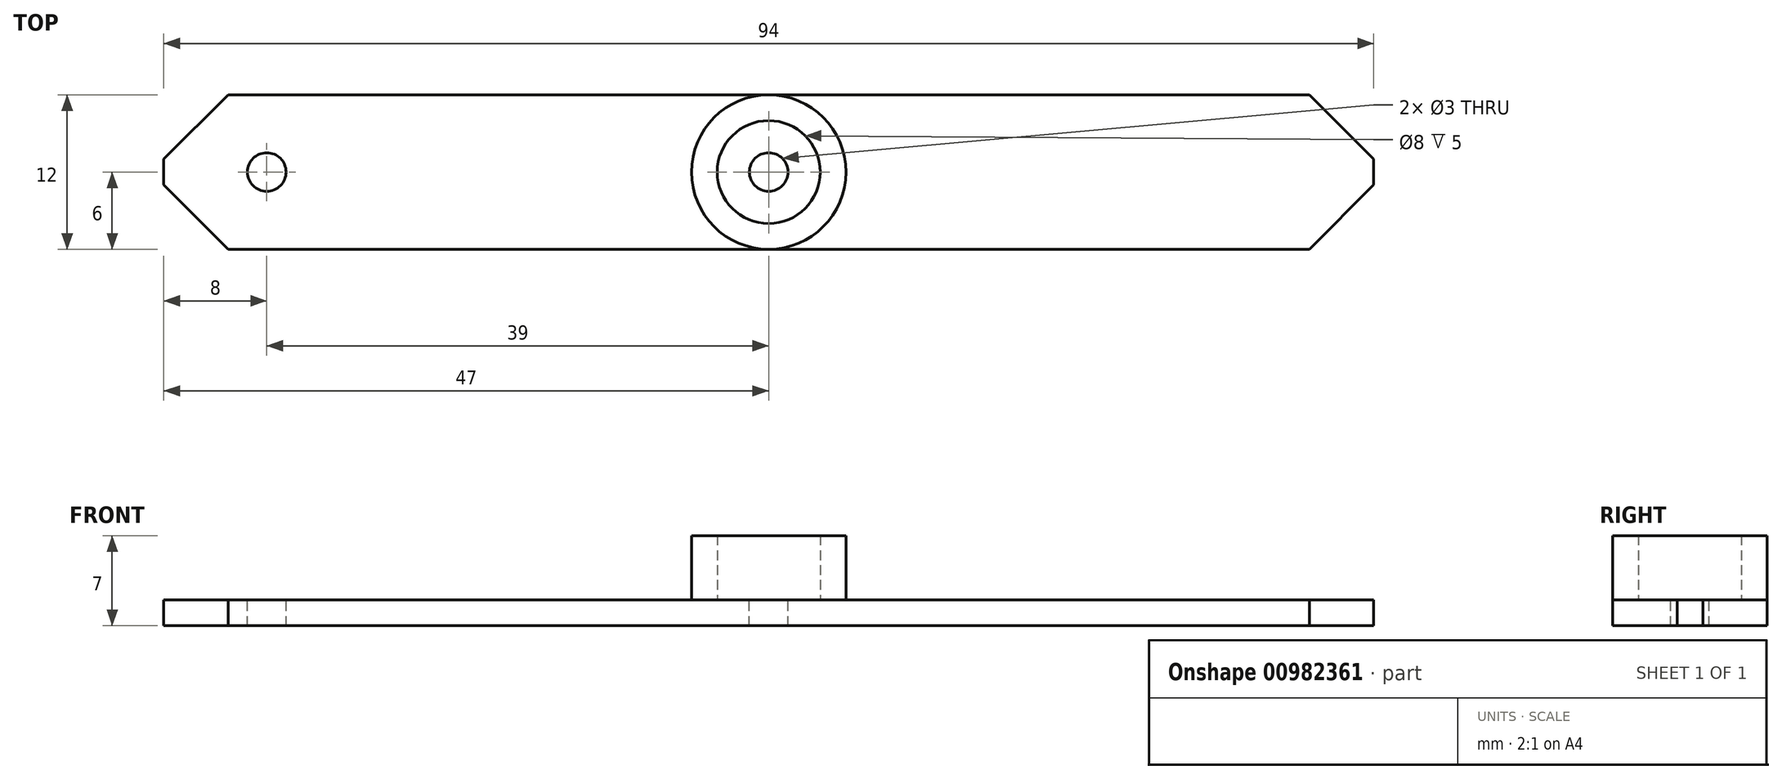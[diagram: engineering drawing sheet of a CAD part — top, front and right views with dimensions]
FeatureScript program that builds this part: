
annotation { "Feature Type Name" : "Feature", "Feature Type Description" : "" }
export const myFeature = defineFeature(function(context is Context, id is Id, definition is map)
    precondition{}
    {
        {
            var Q0;
            Q0=qCreatedBy(makeId("Top.planeOp"),FACE);
            var sketch = newSketch(context, id + "F0", { "sketchPlane" : qUnion([Q0])});
            skLineSegment(sketch, "E0.bottom", {"start": v(0, 0) * mm, "end": v(-94, 0) * mm});
            skLineSegment(sketch, "E0.top", {"start": v(0, -12) * mm, "end": v(-94, -12) * mm});
            skLineSegment(sketch, "E0.left", {"start": v(0, 0) * mm, "end": v(0, -12) * mm});
            skLineSegment(sketch, "E0.right", {"start": v(-94, 0) * mm, "end": v(-94, -12) * mm});
            skSolve(sketch);
        }
        {
            var Q0;
            Q0 = qSketchRegion(id + "F0", true);
            extrude(context, id + "F1", {"entities" : qUnion([Q0]), "depth" : 2 * mm, "offsetDistance" : 25 * mm});
        }
        {
            var Q0;
            Q0=makeQuery(id+"F1.opExtrude","CAP_FACE",FACE,{"disambiguationData":[OSD([sQuery(id+"F0.wireOp",EDGE,"E0.bottom"),sQuery(id+"F0.wireOp",EDGE,"E0.top"),sQuery(id+"F0.wireOp",EDGE,"E0.left"),sQuery(id+"F0.wireOp",EDGE,"E0.right")])],"isStart":false});
            var sketch = newSketch(context, id + "F2", { "sketchPlane" : qUnion([Q0])});
            skCircle(sketch, "E1", {"center": v(-47, -6) * mm, "radius": 6 * mm});
            skPoint(sketch, "E1.centerSnap0", {"position": v(-47, 0) * mm});
            skPoint(sketch, "E1.centerSnap1", {"position": v(0, -6) * mm});
            skSolve(sketch);
        }
        {
            var Q0;
            {var subQ0=sQuery(id+"F2.wireOp",EDGE,"E1");var subQ1=makeQuery(id+"F2.imprint","INTERSECT",VERTEX,{"derivedFrom":[makeQuery(id+"F1.opExtrude","CAP_EDGE",EDGE,{"disambiguationData":[OSD([sQuery(id+"F0.wireOp",EDGE,"E0.bottom")])],"isStart":false}),subQ0]});Q0=makeQuery(id+"F2.imprint","IMPRINT",FACE,{"disambiguationData":[TD([[makeQuery(id+"F2.imprint","IMPRINT",EDGE,{"disambiguationData":[TD([[subQ1,-1.0]])],"derivedFrom":subQ0}),1.0]])]});}
            extrude(context, id + "F3", {"entities" : qUnion([Q0]), "operationType" : NewBodyOperationType.ADD, "depth" : 5 * mm, "offsetDistance" : 25 * mm});
        }
        {
            var Q0;
            Q0=makeQuery(id+"F3.opExtrude","CAP_FACE",FACE,{"disambiguationData":[OSD([sQuery(id+"F2.wireOp",EDGE,"E1")])],"isStart":false});
            shell(context, id + "F4", {"entities" : qUnion([Q0]), "thickness" : 2 * mm});
        }
        {
            var Q0;
            Q0=makeQuery(id+"F1.opExtrude","SWEPT_EDGE",EDGE,{"disambiguationData":[OSD([sQuery(id+"F0.wireOp",EDGE,"E0.top"),sQuery(id+"F0.wireOp",EDGE,"E0.right")])]});
            var Q1;
            Q1=makeQuery(id+"F1.opExtrude","SWEPT_EDGE",EDGE,{"disambiguationData":[OSD([sQuery(id+"F0.wireOp",EDGE,"E0.bottom"),sQuery(id+"F0.wireOp",EDGE,"E0.right")])]});
            var Q2;
            Q2=makeQuery(id+"F1.opExtrude","SWEPT_EDGE",EDGE,{"disambiguationData":[OSD([sQuery(id+"F0.wireOp",EDGE,"E0.bottom"),sQuery(id+"F0.wireOp",EDGE,"E0.left")])]});
            var Q3;
            Q3=makeQuery(id+"F1.opExtrude","SWEPT_EDGE",EDGE,{"disambiguationData":[OSD([sQuery(id+"F0.wireOp",EDGE,"E0.top"),sQuery(id+"F0.wireOp",EDGE,"E0.left")])]});
            chamfer(context, id + "F5", {"entities" : qUnion([Q0, Q1, Q2, Q3]), "width" : 5 * mm, "tangentPropagation" : true});
        }
        {
            var Q0;
            Q0=makeQuery(id+"F4.opShell","OFFSET_FACE",FACE,{"disambiguationData":[OSD([sQuery(id+"F0.wireOp",EDGE,"E0.bottom"),sQuery(id+"F0.wireOp",EDGE,"E0.top"),sQuery(id+"F0.wireOp",EDGE,"E0.left"),sQuery(id+"F0.wireOp",EDGE,"E0.right")])]});
            var sketch = newSketch(context, id + "F6", { "sketchPlane" : qUnion([Q0])});
            skCircle(sketch, "E2", {"center": v(-47, -6) * mm, "radius": 1.5 * mm});
            skSolve(sketch);
        }
        {
            var Q0;
            Q0=makeQuery(id+"F6.imprint","IMPRINT",FACE,{"disambiguationData":[TD([[makeQuery(id+"F6.imprint","IMPRINT",EDGE,{"derivedFrom":sQuery(id+"F6.wireOp",EDGE,"E2")}),1.0]])]});
            extrude(context, id + "F7", {"entities" : qUnion([Q0]), "operationType" : NewBodyOperationType.REMOVE, "oppositeDirection" : true, "depth" : 25 * mm, "offsetDistance" : 25 * mm});
        }
        {
            var Q0;
            {var subQ0=sQuery(id+"F0.wireOp",EDGE,"E0.top");var subQ1=sQuery(id+"F0.wireOp",EDGE,"E0.right");var subQ2=sQuery(id+"F0.wireOp",EDGE,"E0.bottom");var subQ3=makeQuery(id+"F1.opExtrude","CAP_FACE",FACE,{"disambiguationData":[OSD([subQ2,subQ0,sQuery(id+"F0.wireOp",EDGE,"E0.left"),subQ1])],"isStart":false});Q0=makeQuery(id+"F3.boolean.opBoolean","SPLIT",FACE,{"disambiguationData":[TD([makeQuery(id+"F1.opExtrude","SWEPT_FACE",FACE,{"disambiguationData":[OSD([subQ1])]})])],"derivedFrom":subQ3});}
            var sketch = newSketch(context, id + "F8", { "sketchPlane" : qUnion([Q0])});
            skLineSegment(sketch, "E3", {"start": v(-94, -6) * mm, "end": v(-86, -6) * mm, "construction": true});
            skLineSegment(sketch, "E4", {"start": v(-47, 0) * mm, "end": v(-47, -12) * mm, "construction": true});
            skCircle(sketch, "E5", {"center": v(-86, -6) * mm, "radius": 2.85 * mm, "construction": true});
            skCircle(sketch, "E6", {"center": v(-86, -6) * mm, "radius": 1.5 * mm});
            skCircle(sketch, "E7.MirrorC", {"center": v(-8, -6) * mm, "radius": 1.5 * mm});
            skSolve(sketch);
        }
        {
            var Q0;
            Q0=makeQuery(id+"F8.imprint","IMPRINT",FACE,{"disambiguationData":[TD([[makeQuery(id+"F8.imprint","IMPRINT",EDGE,{"derivedFrom":sQuery(id+"F8.wireOp",EDGE,"E7.MirrorC")}),-1.0]])]});
            var Q1;
            Q1=makeQuery(id+"F8.imprint","IMPRINT",FACE,{"disambiguationData":[TD([[makeQuery(id+"F8.imprint","IMPRINT",EDGE,{"derivedFrom":sQuery(id+"F8.wireOp",EDGE,"E6")}),1.0]])]});
            extrude(context, id + "F9", {"entities" : qUnion([Q0, Q1]), "operationType" : NewBodyOperationType.REMOVE, "oppositeDirection" : true, "depth" : 25 * mm, "offsetDistance" : 25 * mm});
        }
    });
